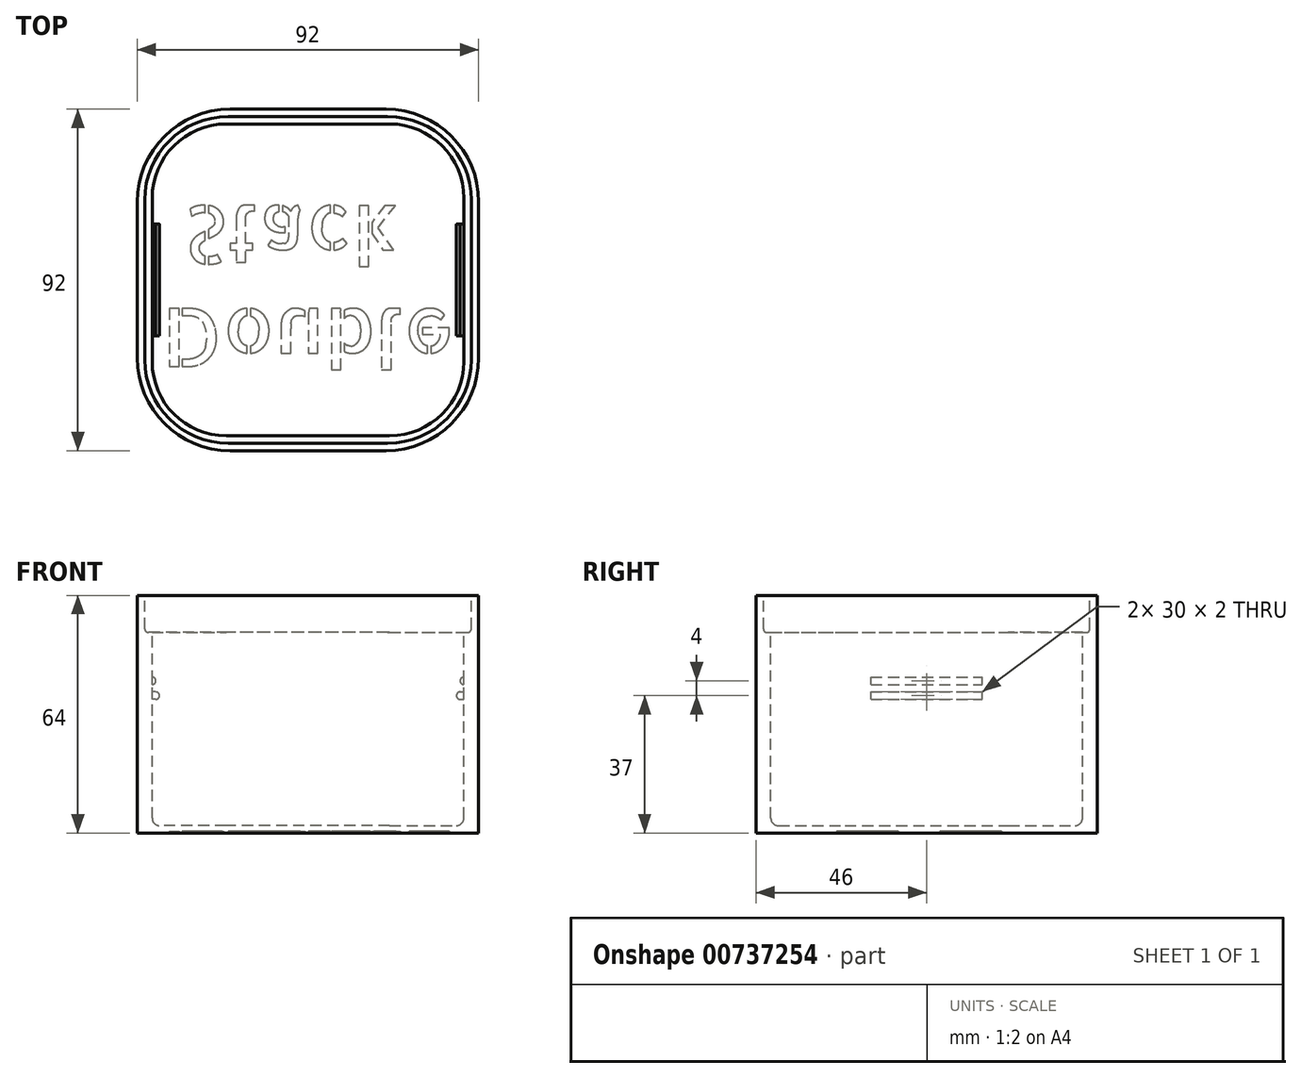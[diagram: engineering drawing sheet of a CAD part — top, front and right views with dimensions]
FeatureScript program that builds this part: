
annotation { "Feature Type Name" : "Feature", "Feature Type Description" : "" }
export const myFeature = defineFeature(function(context is Context, id is Id, definition is map)
    precondition{}
    {
        {
            var Q0;
            Q0=qCreatedBy(makeId("Top.planeOp"),FACE);
            var sketch = newSketch(context, id + "F0", { "sketchPlane" : qUnion([Q0])});
            skLineSegment(sketch, "E0.bottom", {"start": v(21, -46) * mm, "end": v(-21, -46) * mm});
            skLineSegment(sketch, "E0.top", {"start": v(21, 46) * mm, "end": v(-21, 46) * mm});
            skLineSegment(sketch, "E0.left", {"start": v(46, -21) * mm, "end": v(46, 21) * mm});
            skLineSegment(sketch, "E0.right", {"start": v(-46, -21) * mm, "end": v(-46, 21) * mm});
            skPoint(sketch, "E0.middle", {"position": v(0, 0) * mm});
            skPoint(sketch, "E1.visualSharp", {"position": v(46, -46) * mm});
            skArc(sketch, "E1.filletArc", {"start": v(21, -46) * mm, "mid": v(38.68, -38.68) * mm, "end": v(46, -21) * mm});
            skPoint(sketch, "E2.visualSharp", {"position": v(46, 46) * mm});
            skArc(sketch, "E2.filletArc", {"start": v(46, 21) * mm, "mid": v(38.68, 38.68) * mm, "end": v(21, 46) * mm});
            skPoint(sketch, "E3.visualSharp", {"position": v(-46, 46) * mm});
            skArc(sketch, "E3.filletArc", {"start": v(-21, 46) * mm, "mid": v(-38.68, 38.68) * mm, "end": v(-46, 21) * mm});
            skPoint(sketch, "E4.visualSharp", {"position": v(-46, -46) * mm});
            skArc(sketch, "E4.filletArc", {"start": v(-46, -21) * mm, "mid": v(-38.68, -38.68) * mm, "end": v(-21, -46) * mm});
            skSolve(sketch);
        }
        {
            var Q0;
            Q0=makeQuery(id+"F0.imprint","IMPRINT",FACE,{"disambiguationData":[TD([[makeQuery(id+"F0.imprint","IMPRINT",EDGE,{"derivedFrom":sQuery(id+"F0.wireOp",EDGE,"E0.bottom")}),-1.0]])]});
            extrude(context, id + "F1", {"entities" : qUnion([Q0]), "depth" : 64 * mm, "offsetDistance" : 25 * mm});
        }
        {
            var Q0;
            Q0=makeQuery(id+"F1.opExtrude","CAP_FACE",FACE,{"disambiguationData":[OSD([sQuery(id+"F0.wireOp",EDGE,"E0.bottom"),sQuery(id+"F0.wireOp",EDGE,"E0.top"),sQuery(id+"F0.wireOp",EDGE,"E0.left"),sQuery(id+"F0.wireOp",EDGE,"E0.right"),sQuery(id+"F0.wireOp",EDGE,"E1.filletArc"),sQuery(id+"F0.wireOp",EDGE,"E2.filletArc"),sQuery(id+"F0.wireOp",EDGE,"E3.filletArc"),sQuery(id+"F0.wireOp",EDGE,"E4.filletArc")])],"isStart":false});
            var sketch = newSketch(context, id + "F2", { "sketchPlane" : qUnion([Q0])});
            skLineSegment(sketch, "E5.bottom", {"start": v(21.5, -44) * mm, "end": v(-21.5, -44) * mm});
            skLineSegment(sketch, "E5.top", {"start": v(21.5, 44) * mm, "end": v(-21.5, 44) * mm});
            skLineSegment(sketch, "E5.left", {"start": v(44, -21.5) * mm, "end": v(44, 21.5) * mm});
            skLineSegment(sketch, "E5.right", {"start": v(-44, -21.5) * mm, "end": v(-44, 21.5) * mm});
            skPoint(sketch, "E5.middle", {"position": v(0, 0) * mm});
            skPoint(sketch, "E6.visualSharp", {"position": v(-44, 44) * mm});
            skArc(sketch, "E6.filletArc", {"start": v(-21.5, 44) * mm, "mid": v(-37.4, 37.4) * mm, "end": v(-44, 21.5) * mm});
            skPoint(sketch, "E7.visualSharp", {"position": v(44, 44) * mm});
            skArc(sketch, "E7.filletArc", {"start": v(44, 21.5) * mm, "mid": v(37.4, 37.4) * mm, "end": v(21.5, 44) * mm});
            skPoint(sketch, "E8.visualSharp", {"position": v(44, -44) * mm});
            skArc(sketch, "E8.filletArc", {"start": v(21.5, -44) * mm, "mid": v(37.4, -37.4) * mm, "end": v(44, -21.5) * mm});
            skPoint(sketch, "E9.visualSharp", {"position": v(-44, -44) * mm});
            skArc(sketch, "E9.filletArc", {"start": v(-44, -21.5) * mm, "mid": v(-37.4, -37.4) * mm, "end": v(-21.5, -44) * mm});
            skSolve(sketch);
        }
        {
            var Q0;
            Q0=makeQuery(id+"F2.imprint","IMPRINT",FACE,{"disambiguationData":[TD([[makeQuery(id+"F2.imprint","IMPRINT",EDGE,{"derivedFrom":sQuery(id+"F2.wireOp",EDGE,"E5.bottom")}),-1.0]])]});
            extrude(context, id + "F3", {"entities" : qUnion([Q0]), "operationType" : NewBodyOperationType.REMOVE, "oppositeDirection" : true, "depth" : 10 * mm, "offsetDistance" : 25 * mm});
        }
        {
            var Q0;
            Q0=makeQuery(id+"F3.boolean.opBoolean","COPY",FACE,{"derivedFrom":makeQuery(id+"F3.opExtrude","CAP_FACE",FACE,{"disambiguationData":[OSD([sQuery(id+"F2.wireOp",EDGE,"E5.bottom"),sQuery(id+"F2.wireOp",EDGE,"E5.top"),sQuery(id+"F2.wireOp",EDGE,"E5.left"),sQuery(id+"F2.wireOp",EDGE,"E5.right"),sQuery(id+"F2.wireOp",EDGE,"E6.filletArc"),sQuery(id+"F2.wireOp",EDGE,"E7.filletArc"),sQuery(id+"F2.wireOp",EDGE,"E8.filletArc"),sQuery(id+"F2.wireOp",EDGE,"E9.filletArc")])],"isStart":false})});
            var sketch = newSketch(context, id + "F4", { "sketchPlane" : qUnion([Q0])});
            skLineSegment(sketch, "E10.bottom", {"start": v(22, -42) * mm, "end": v(-22, -42) * mm});
            skLineSegment(sketch, "E10.top", {"start": v(22, 42) * mm, "end": v(-22, 42) * mm});
            skLineSegment(sketch, "E10.left", {"start": v(42, -22) * mm, "end": v(42, 22) * mm});
            skLineSegment(sketch, "E10.right", {"start": v(-42, -22) * mm, "end": v(-42, 22) * mm});
            skPoint(sketch, "E10.middle", {"position": v(0, 0) * mm});
            skPoint(sketch, "E11.visualSharp", {"position": v(-42, 42) * mm});
            skArc(sketch, "E11.filletArc", {"start": v(-22, 42) * mm, "mid": v(-36.14, 36.14) * mm, "end": v(-42, 22) * mm});
            skPoint(sketch, "E12.visualSharp", {"position": v(42, 42) * mm});
            skArc(sketch, "E12.filletArc", {"start": v(42, 22) * mm, "mid": v(36.14, 36.14) * mm, "end": v(22, 42) * mm});
            skPoint(sketch, "E13.visualSharp", {"position": v(42, -42) * mm});
            skArc(sketch, "E13.filletArc", {"start": v(22, -42) * mm, "mid": v(36.14, -36.14) * mm, "end": v(42, -22) * mm});
            skPoint(sketch, "E14.visualSharp", {"position": v(-42, -42) * mm});
            skArc(sketch, "E14.filletArc", {"start": v(-42, -22) * mm, "mid": v(-36.14, -36.14) * mm, "end": v(-22, -42) * mm});
            skSolve(sketch);
        }
        {
            var Q0;
            Q0=makeQuery(id+"F4.imprint","IMPRINT",FACE,{"disambiguationData":[TD([[makeQuery(id+"F4.imprint","IMPRINT",EDGE,{"derivedFrom":sQuery(id+"F4.wireOp",EDGE,"E10.bottom")}),-1.0]])]});
            extrude(context, id + "F5", {"entities" : qUnion([Q0]), "operationType" : NewBodyOperationType.REMOVE, "oppositeDirection" : true, "depth" : 52 * mm, "offsetDistance" : 25 * mm});
        }
        {
            var Q0;
            Q0=makeQuery(id+"F3.boolean.opBoolean","COPY",EDGE,{"derivedFrom":makeQuery(id+"F3.opExtrude","CAP_EDGE",EDGE,{"disambiguationData":[OSD([sQuery(id+"F2.wireOp",EDGE,"E5.left")])],"isStart":false})});
            var Q1;
            Q1=makeQuery(id+"F3.boolean.opBoolean","COPY",EDGE,{"derivedFrom":makeQuery(id+"F3.opExtrude","CAP_EDGE",EDGE,{"disambiguationData":[OSD([sQuery(id+"F2.wireOp",EDGE,"E7.filletArc")])],"isStart":false})});
            var Q2;
            Q2=makeQuery(id+"F3.boolean.opBoolean","COPY",EDGE,{"derivedFrom":makeQuery(id+"F3.opExtrude","CAP_EDGE",EDGE,{"disambiguationData":[OSD([sQuery(id+"F2.wireOp",EDGE,"E5.top")])],"isStart":false})});
            var Q3;
            Q3=makeQuery(id+"F3.boolean.opBoolean","COPY",EDGE,{"derivedFrom":makeQuery(id+"F3.opExtrude","CAP_EDGE",EDGE,{"disambiguationData":[OSD([sQuery(id+"F2.wireOp",EDGE,"E6.filletArc")])],"isStart":false})});
            var Q4;
            Q4=makeQuery(id+"F3.boolean.opBoolean","COPY",EDGE,{"derivedFrom":makeQuery(id+"F3.opExtrude","CAP_EDGE",EDGE,{"disambiguationData":[OSD([sQuery(id+"F2.wireOp",EDGE,"E5.right")])],"isStart":false})});
            var Q5;
            Q5=makeQuery(id+"F3.boolean.opBoolean","COPY",EDGE,{"derivedFrom":makeQuery(id+"F3.opExtrude","CAP_EDGE",EDGE,{"disambiguationData":[OSD([sQuery(id+"F2.wireOp",EDGE,"E9.filletArc")])],"isStart":false})});
            var Q6;
            Q6=makeQuery(id+"F3.boolean.opBoolean","COPY",EDGE,{"derivedFrom":makeQuery(id+"F3.opExtrude","CAP_EDGE",EDGE,{"disambiguationData":[OSD([sQuery(id+"F2.wireOp",EDGE,"E5.bottom")])],"isStart":false})});
            var Q7;
            Q7=makeQuery(id+"F3.boolean.opBoolean","COPY",EDGE,{"derivedFrom":makeQuery(id+"F3.opExtrude","CAP_EDGE",EDGE,{"disambiguationData":[OSD([sQuery(id+"F2.wireOp",EDGE,"E8.filletArc")])],"isStart":false})});
            var Q8;
            Q8=makeQuery(id+"F3.boolean.opBoolean","COPY",EDGE,{"derivedFrom":makeQuery(id+"F3.opExtrude","CAP_EDGE",EDGE,{"disambiguationData":[OSD([sQuery(id+"F2.wireOp",EDGE,"E5.bottom")])],"isStart":true})});
            var Q9;
            Q9=makeQuery(id+"F3.boolean.opBoolean","COPY",EDGE,{"derivedFrom":makeQuery(id+"F3.opExtrude","CAP_EDGE",EDGE,{"disambiguationData":[OSD([sQuery(id+"F2.wireOp",EDGE,"E9.filletArc")])],"isStart":true})});
            var Q10;
            Q10=makeQuery(id+"F3.boolean.opBoolean","COPY",EDGE,{"derivedFrom":makeQuery(id+"F3.opExtrude","CAP_EDGE",EDGE,{"disambiguationData":[OSD([sQuery(id+"F2.wireOp",EDGE,"E8.filletArc")])],"isStart":true})});
            var Q11;
            Q11=makeQuery(id+"F3.boolean.opBoolean","COPY",EDGE,{"derivedFrom":makeQuery(id+"F3.opExtrude","CAP_EDGE",EDGE,{"disambiguationData":[OSD([sQuery(id+"F2.wireOp",EDGE,"E5.right")])],"isStart":true})});
            var Q12;
            Q12=makeQuery(id+"F3.boolean.opBoolean","COPY",EDGE,{"derivedFrom":makeQuery(id+"F3.opExtrude","CAP_EDGE",EDGE,{"disambiguationData":[OSD([sQuery(id+"F2.wireOp",EDGE,"E6.filletArc")])],"isStart":true})});
            var Q13;
            Q13=makeQuery(id+"F3.boolean.opBoolean","COPY",EDGE,{"derivedFrom":makeQuery(id+"F3.opExtrude","CAP_EDGE",EDGE,{"disambiguationData":[OSD([sQuery(id+"F2.wireOp",EDGE,"E5.top")])],"isStart":true})});
            var Q14;
            Q14=makeQuery(id+"F3.boolean.opBoolean","COPY",EDGE,{"derivedFrom":makeQuery(id+"F3.opExtrude","CAP_EDGE",EDGE,{"disambiguationData":[OSD([sQuery(id+"F2.wireOp",EDGE,"E7.filletArc")])],"isStart":true})});
            var Q15;
            Q15=makeQuery(id+"F3.boolean.opBoolean","COPY",EDGE,{"derivedFrom":makeQuery(id+"F3.opExtrude","CAP_EDGE",EDGE,{"disambiguationData":[OSD([sQuery(id+"F2.wireOp",EDGE,"E5.left")])],"isStart":true})});
            fillet(context, id + "F6", {"entities" : qUnion([Q0, Q1, Q2, Q3, Q4, Q5, Q6, Q7, Q8, Q9, Q10, Q11, Q12, Q13, Q14, Q15]), "radius" : 1 * mm, "tangentPropagation" : true, "allowEdgeOverflow" : false});
        }
        {
            var Q0;
            Q0=makeQuery(id+"F5.boolean.opBoolean","COPY",FACE,{"derivedFrom":makeQuery(id+"F5.opExtrude","SWEPT_FACE",FACE,{"disambiguationData":[OSD([sQuery(id+"F4.wireOp",EDGE,"E10.right")])]})});
            var sketch = newSketch(context, id + "F7", { "sketchPlane" : qUnion([Q0])});
            skLineSegment(sketch, "E15.bottom", {"start": v(15, 36) * mm, "end": v(-15, 36) * mm});
            skLineSegment(sketch, "E15.top", {"start": v(15, 38) * mm, "end": v(-15, 38) * mm});
            skLineSegment(sketch, "E15.left", {"start": v(15, 36) * mm, "end": v(15, 38) * mm});
            skLineSegment(sketch, "E15.right", {"start": v(-15, 36) * mm, "end": v(-15, 38) * mm});
            skPoint(sketch, "E15.middle", {"position": v(0, 37) * mm});
            skLineSegment(sketch, "E16.bottom", {"start": v(15, 40) * mm, "end": v(-15, 40) * mm});
            skLineSegment(sketch, "E16.top", {"start": v(15, 42) * mm, "end": v(-15, 42) * mm});
            skLineSegment(sketch, "E16.left", {"start": v(15, 40) * mm, "end": v(15, 42) * mm});
            skLineSegment(sketch, "E16.right", {"start": v(-15, 40) * mm, "end": v(-15, 42) * mm});
            skPoint(sketch, "E16.middle", {"position": v(0, 41) * mm});
            skSolve(sketch);
        }
        {
            var Q0;
            Q0=makeQuery(id+"F7.imprint","IMPRINT",FACE,{"disambiguationData":[TD([[makeQuery(id+"F7.imprint","IMPRINT",EDGE,{"derivedFrom":sQuery(id+"F7.wireOp",EDGE,"E15.bottom")}),-1.0]])]});
            extrude(context, id + "F8", {"entities" : qUnion([Q0]), "operationType" : NewBodyOperationType.ADD, "depth" : 2 * mm, "offsetDistance" : 25 * mm});
        }
        {
            var Q0;
            Q0=makeQuery(id+"F8.opExtrude","CAP_EDGE",EDGE,{"disambiguationData":[OSD([sQuery(id+"F7.wireOp",EDGE,"E15.top")])],"isStart":true});
            var Q1;
            Q1=makeQuery(id+"F8.opExtrude","CAP_EDGE",EDGE,{"disambiguationData":[OSD([sQuery(id+"F7.wireOp",EDGE,"E15.bottom")])],"isStart":true});
            var Q2;
            Q2=makeQuery(id+"F8.opExtrude","CAP_EDGE",EDGE,{"disambiguationData":[OSD([sQuery(id+"F7.wireOp",EDGE,"E15.top")])],"isStart":false});
            var Q3;
            Q3=makeQuery(id+"F8.opExtrude","CAP_EDGE",EDGE,{"disambiguationData":[OSD([sQuery(id+"F7.wireOp",EDGE,"E15.bottom")])],"isStart":false});
            fillet(context, id + "F9", {"entities" : qUnion([Q0, Q1, Q2, Q3]), "radius" : 1 * mm, "tangentPropagation" : true, "allowEdgeOverflow" : false});
        }
        {
            var Q0;
            Q0=makeQuery(id+"F7.imprint","IMPRINT",FACE,{"disambiguationData":[TD([[makeQuery(id+"F7.imprint","IMPRINT",EDGE,{"derivedFrom":sQuery(id+"F7.wireOp",EDGE,"E16.bottom")}),-1.0]])]});
            extrude(context, id + "F10", {"entities" : qUnion([Q0]), "operationType" : NewBodyOperationType.ADD, "depth" : 1 * mm, "offsetDistance" : 25 * mm});
        }
        {
            var Q0;
            Q0=makeQuery(id+"F10.opExtrude","CAP_EDGE",EDGE,{"disambiguationData":[OSD([sQuery(id+"F7.wireOp",EDGE,"E16.top")])],"isStart":false});
            var Q1;
            Q1=makeQuery(id+"F10.opExtrude","CAP_EDGE",EDGE,{"disambiguationData":[OSD([sQuery(id+"F7.wireOp",EDGE,"E16.bottom")])],"isStart":false});
            fillet(context, id + "F11", {"entities" : qUnion([Q0, Q1]), "radius" : 1 * mm, "tangentPropagation" : true, "allowEdgeOverflow" : false});
        }
        {
            var Q0;
            Q0=makeQuery(id+"F5.boolean.opBoolean","COPY",FACE,{"derivedFrom":makeQuery(id+"F5.opExtrude","SWEPT_FACE",FACE,{"disambiguationData":[OSD([sQuery(id+"F4.wireOp",EDGE,"E10.left")])]})});
            var sketch = newSketch(context, id + "F12", { "sketchPlane" : qUnion([Q0])});
            skLineSegment(sketch, "E17.bottom", {"start": v(15, 36) * mm, "end": v(-15, 36) * mm});
            skLineSegment(sketch, "E17.top", {"start": v(15, 38) * mm, "end": v(-15, 38) * mm});
            skLineSegment(sketch, "E17.left", {"start": v(15, 36) * mm, "end": v(15, 38) * mm});
            skLineSegment(sketch, "E17.right", {"start": v(-15, 36) * mm, "end": v(-15, 38) * mm});
            skPoint(sketch, "E17.middle", {"position": v(0, 37) * mm});
            skPoint(sketch, "E17.middle.positionSnap0", {"position": v(0, 2) * mm});
            skPoint(sketch, "E17.centerSnap0", {"position": v(0, 2) * mm});
            skLineSegment(sketch, "E18.bottom", {"start": v(15, 40) * mm, "end": v(-15, 40) * mm});
            skLineSegment(sketch, "E18.top", {"start": v(15, 42) * mm, "end": v(-15, 42) * mm});
            skLineSegment(sketch, "E18.left", {"start": v(15, 40) * mm, "end": v(15, 42) * mm});
            skLineSegment(sketch, "E18.right", {"start": v(-15, 40) * mm, "end": v(-15, 42) * mm});
            skPoint(sketch, "E18.middle", {"position": v(0, 41) * mm});
            skSolve(sketch);
        }
        {
            var Q0;
            Q0=makeQuery(id+"F12.imprint","IMPRINT",FACE,{"disambiguationData":[TD([[makeQuery(id+"F12.imprint","IMPRINT",EDGE,{"derivedFrom":sQuery(id+"F12.wireOp",EDGE,"E17.bottom")}),-1.0]])]});
            extrude(context, id + "F13", {"entities" : qUnion([Q0]), "operationType" : NewBodyOperationType.ADD, "depth" : 2 * mm, "offsetDistance" : 25 * mm});
        }
        {
            var Q0;
            Q0=makeQuery(id+"F13.opExtrude","CAP_EDGE",EDGE,{"disambiguationData":[OSD([sQuery(id+"F12.wireOp",EDGE,"E17.top")])],"isStart":true});
            var Q1;
            Q1=makeQuery(id+"F13.opExtrude","CAP_EDGE",EDGE,{"disambiguationData":[OSD([sQuery(id+"F12.wireOp",EDGE,"E17.bottom")])],"isStart":true});
            var Q2;
            Q2=makeQuery(id+"F13.opExtrude","CAP_EDGE",EDGE,{"disambiguationData":[OSD([sQuery(id+"F12.wireOp",EDGE,"E17.top")])],"isStart":false});
            var Q3;
            Q3=makeQuery(id+"F13.opExtrude","CAP_EDGE",EDGE,{"disambiguationData":[OSD([sQuery(id+"F12.wireOp",EDGE,"E17.bottom")])],"isStart":false});
            fillet(context, id + "F14", {"entities" : qUnion([Q0, Q1, Q2, Q3]), "radius" : 1 * mm, "tangentPropagation" : true, "allowEdgeOverflow" : false});
        }
        {
            var Q0;
            Q0=makeQuery(id+"F12.imprint","IMPRINT",FACE,{"disambiguationData":[TD([[makeQuery(id+"F12.imprint","IMPRINT",EDGE,{"derivedFrom":sQuery(id+"F12.wireOp",EDGE,"E18.bottom")}),-1.0]])]});
            extrude(context, id + "F15", {"entities" : qUnion([Q0]), "operationType" : NewBodyOperationType.ADD, "depth" : 1 * mm, "offsetDistance" : 25 * mm});
        }
        {
            var Q0;
            Q0=makeQuery(id+"F15.opExtrude","CAP_EDGE",EDGE,{"disambiguationData":[OSD([sQuery(id+"F12.wireOp",EDGE,"E18.top")])],"isStart":false});
            var Q1;
            Q1=makeQuery(id+"F15.opExtrude","CAP_EDGE",EDGE,{"disambiguationData":[OSD([sQuery(id+"F12.wireOp",EDGE,"E18.bottom")])],"isStart":false});
            fillet(context, id + "F16", {"entities" : qUnion([Q0, Q1]), "radius" : 1 * mm, "tangentPropagation" : true, "allowEdgeOverflow" : false});
        }
        {
            var Q0;
            Q0=makeQuery(id+"F5.boolean.opBoolean","COPY",FACE,{"derivedFrom":makeQuery(id+"F5.opExtrude","CAP_FACE",FACE,{"disambiguationData":[OSD([sQuery(id+"F4.wireOp",EDGE,"E10.bottom"),sQuery(id+"F4.wireOp",EDGE,"E10.top"),sQuery(id+"F4.wireOp",EDGE,"E10.left"),sQuery(id+"F4.wireOp",EDGE,"E10.right"),sQuery(id+"F4.wireOp",EDGE,"E11.filletArc"),sQuery(id+"F4.wireOp",EDGE,"E12.filletArc"),sQuery(id+"F4.wireOp",EDGE,"E13.filletArc"),sQuery(id+"F4.wireOp",EDGE,"E14.filletArc")])],"isStart":false})});
            fillet(context, id + "F17", {"entities" : qUnion([Q0]), "radius" : 2 * mm, "tangentPropagation" : true, "allowEdgeOverflow" : false});
        }
        {
            var Q0;
            Q0=makeQuery(id+"F1.opExtrude","CAP_FACE",FACE,{"disambiguationData":[OSD([sQuery(id+"F0.wireOp",EDGE,"E0.bottom"),sQuery(id+"F0.wireOp",EDGE,"E0.top"),sQuery(id+"F0.wireOp",EDGE,"E0.left"),sQuery(id+"F0.wireOp",EDGE,"E0.right"),sQuery(id+"F0.wireOp",EDGE,"E1.filletArc"),sQuery(id+"F0.wireOp",EDGE,"E2.filletArc"),sQuery(id+"F0.wireOp",EDGE,"E3.filletArc"),sQuery(id+"F0.wireOp",EDGE,"E4.filletArc")])],"isStart":true});
            var sketch = newSketch(context, id + "F18", { "sketchPlane" : qUnion([Q0])});
            skText(sketch, "E19", { "text": "Double\n Stack", "fontName": "AllertaStencil-Regular.ttf"});
            const initialGuessF18  = {"E19": [-0.03934, 0.00774, 1, 0, 0.01563]};
            skSetInitialGuess(sketch, initialGuessF18);
            skSolve(sketch);
        }
        {
            var Q0;
            Q0 = qSketchRegion(id + "F18", true);
            extrude(context, id + "F19", {"entities" : qUnion([Q0]), "operationType" : NewBodyOperationType.REMOVE, "oppositeDirection" : true, "depth" : 0.5 * mm, "offsetDistance" : 25 * mm});
        }
    });
